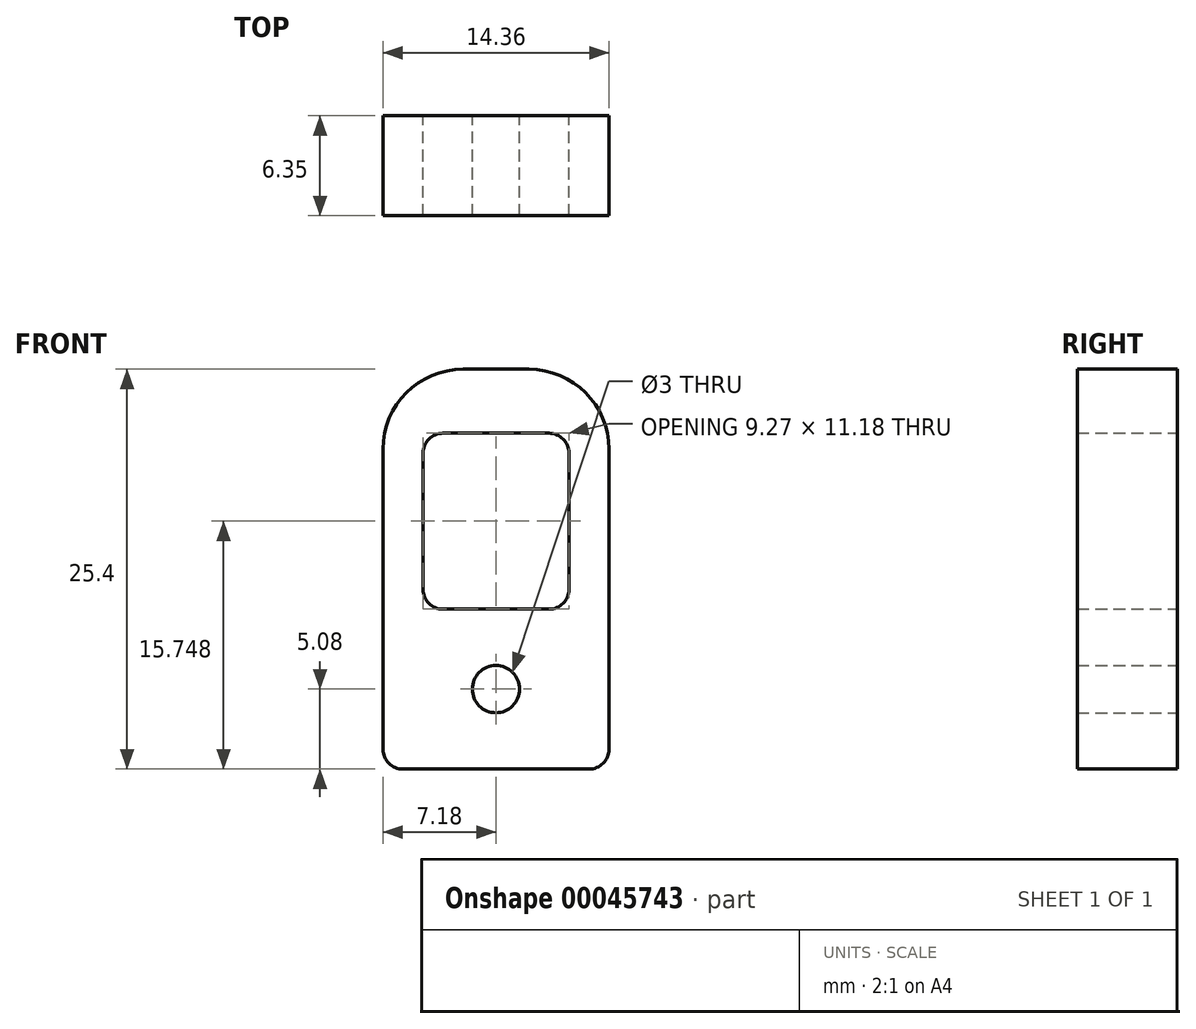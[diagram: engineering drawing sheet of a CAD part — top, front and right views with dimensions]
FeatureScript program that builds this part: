
annotation { "Feature Type Name" : "Feature", "Feature Type Description" : "" }
export const myFeature = defineFeature(function(context is Context, id is Id, definition is map)
    precondition{}
    {
        {
            var Q0;
            Q0=qCreatedBy(makeId("Front.planeOp"),FACE);
            var sketch = newSketch(context, id + "F0", { "sketchPlane" : qUnion([Q0])});
            skCircle(sketch, "E0", {"center": v(0, 0) * mm, "radius": 1.5 * mm});
            skLineSegment(sketch, "E1.bottom", {"start": v(-7.18, 20.32) * mm, "end": v(7.18, 20.32) * mm});
            skLineSegment(sketch, "E1.top", {"start": v(-7.18, -5.08) * mm, "end": v(7.18, -5.08) * mm});
            skLineSegment(sketch, "E1.left", {"start": v(-7.18, 20.32) * mm, "end": v(-7.18, -5.08) * mm});
            skLineSegment(sketch, "E1.right", {"start": v(7.18, 20.32) * mm, "end": v(7.18, -5.08) * mm});
            skLineSegment(sketch, "E2", {"start": v(0, 20.32) * mm, "end": v(0, -5.08) * mm, "construction": true});
            skLineSegment(sketch, "E3.rect.bottom", {"start": v(4.64, 16.26) * mm, "end": v(-4.64, 16.26) * mm});
            skLineSegment(sketch, "E3.rect.top", {"start": v(4.64, 5.08) * mm, "end": v(-4.64, 5.08) * mm});
            skLineSegment(sketch, "E3.rect.left", {"start": v(4.64, 16.26) * mm, "end": v(4.64, 5.08) * mm});
            skLineSegment(sketch, "E3.rect.right", {"start": v(-4.64, 16.26) * mm, "end": v(-4.64, 5.08) * mm});
            skPoint(sketch, "E3.rect.middle", {"position": v(0, 10.67) * mm});
            skSolve(sketch);
        }
        {
            var Q0;
            Q0=makeQuery(id+"F0.imprint","IMPRINT",FACE,{"disambiguationData":[TD([[makeQuery(id+"F0.imprint","IMPRINT",EDGE,{"derivedFrom":sQuery(id+"F0.wireOp",EDGE,"E1.bottom")}),-1.0]])]});
            extrude(context, id + "F1", {"entities" : qUnion([Q0]), "depth" : 6.35 * mm});
        }
        {
            var Q0;
            Q0=makeQuery(id+"F1.opExtrude","SWEPT_EDGE",EDGE,{"disambiguationData":[OSD([sQuery(id+"F0.wireOp",EDGE,"E1.bottom"),sQuery(id+"F0.wireOp",EDGE,"E1.right")])]});
            var Q1;
            Q1=makeQuery(id+"F1.opExtrude","SWEPT_EDGE",EDGE,{"disambiguationData":[OSD([sQuery(id+"F0.wireOp",EDGE,"E1.bottom"),sQuery(id+"F0.wireOp",EDGE,"E1.left")])]});
            fillet(context, id + "F2", {"entities" : qUnion([Q0, Q1]), "radius" : 5.08 * mm, "tangentPropagation" : true, "allowEdgeOverflow" : false});
        }
        {
            var Q0;
            Q0=makeQuery(id+"F1.opExtrude","SWEPT_EDGE",EDGE,{"disambiguationData":[OSD([sQuery(id+"F0.wireOp",EDGE,"E1.top"),sQuery(id+"F0.wireOp",EDGE,"E1.right")])]});
            var Q1;
            Q1=makeQuery(id+"F1.opExtrude","SWEPT_EDGE",EDGE,{"disambiguationData":[OSD([sQuery(id+"F0.wireOp",EDGE,"E1.top"),sQuery(id+"F0.wireOp",EDGE,"E1.left")])]});
            var Q2;
            Q2=makeQuery(id+"F1.opExtrude","SWEPT_EDGE",EDGE,{"disambiguationData":[OSD([sQuery(id+"F0.wireOp",EDGE,"E3.rect.bottom"),sQuery(id+"F0.wireOp",EDGE,"E3.rect.right")])]});
            var Q3;
            Q3=makeQuery(id+"F1.opExtrude","SWEPT_EDGE",EDGE,{"disambiguationData":[OSD([sQuery(id+"F0.wireOp",EDGE,"E3.rect.bottom"),sQuery(id+"F0.wireOp",EDGE,"E3.rect.left")])]});
            var Q4;
            Q4=makeQuery(id+"F1.opExtrude","SWEPT_EDGE",EDGE,{"disambiguationData":[OSD([sQuery(id+"F0.wireOp",EDGE,"E3.rect.top"),sQuery(id+"F0.wireOp",EDGE,"E3.rect.right")])]});
            var Q5;
            Q5=makeQuery(id+"F1.opExtrude","SWEPT_EDGE",EDGE,{"disambiguationData":[OSD([sQuery(id+"F0.wireOp",EDGE,"E3.rect.top"),sQuery(id+"F0.wireOp",EDGE,"E3.rect.left")])]});
            fillet(context, id + "F3", {"entities" : qUnion([Q0, Q1, Q2, Q3, Q4, Q5]), "radius" : 1.27 * mm, "tangentPropagation" : true, "allowEdgeOverflow" : false});
        }
    });
